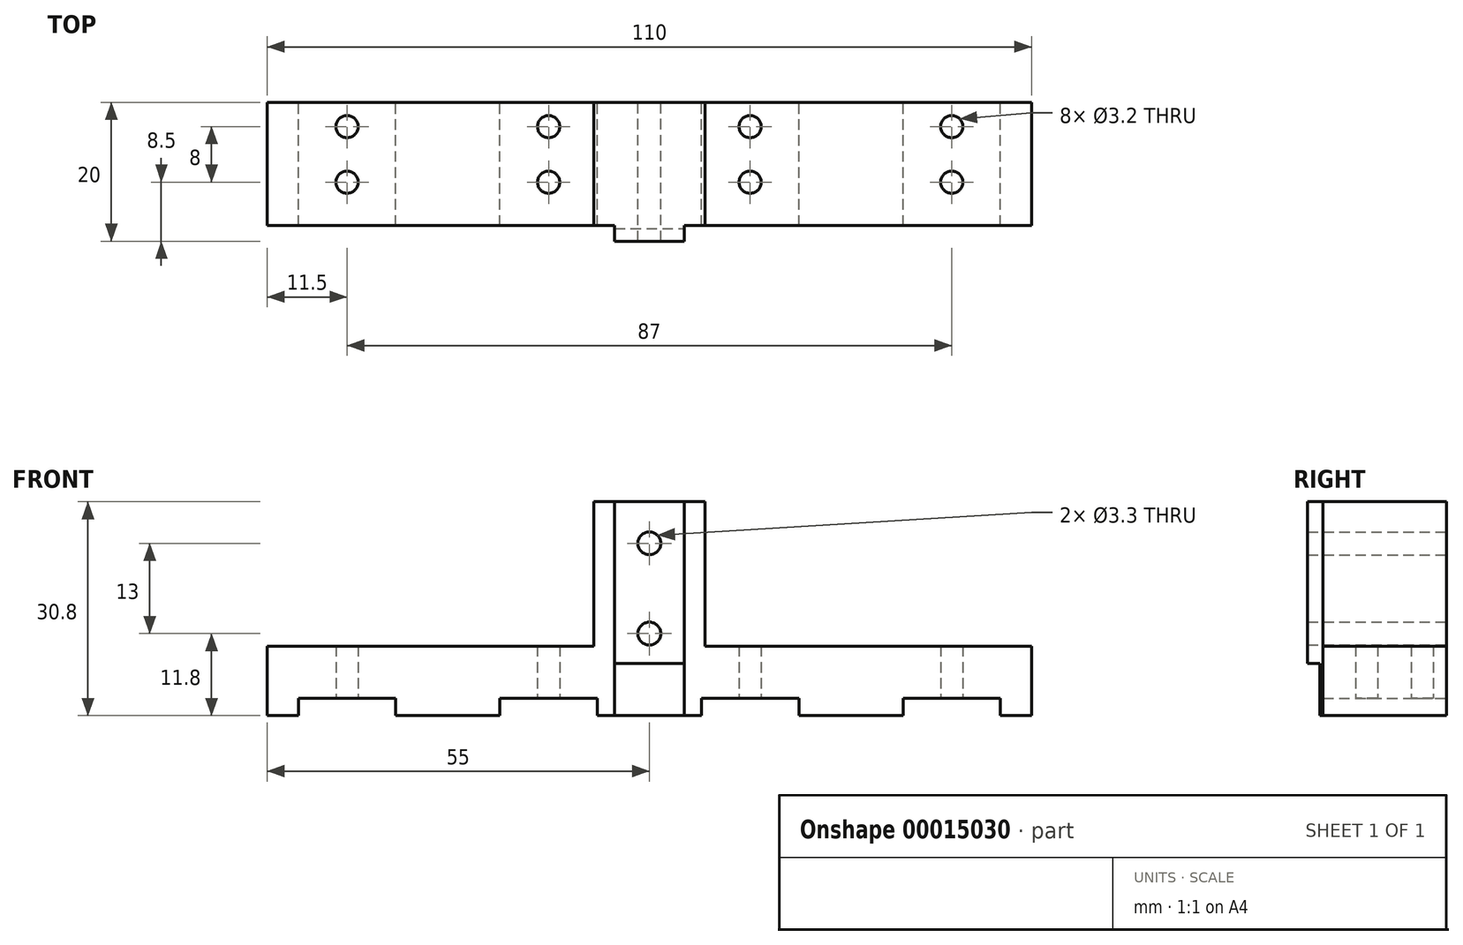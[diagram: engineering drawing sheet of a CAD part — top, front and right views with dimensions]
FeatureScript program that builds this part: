
annotation { "Feature Type Name" : "Feature", "Feature Type Description" : "" }
export const myFeature = defineFeature(function(context is Context, id is Id, definition is map)
    precondition{}
    {
        {
            var Q0;
            Q0=qCreatedBy(makeId("Front.planeOp"),FACE);
            var sketch = newSketch(context, id + "F0", { "sketchPlane" : qUnion([Q0])});
            skLineSegment(sketch, "E0", {"start": v(8, 20.8) * mm, "end": v(-8, 20.8) * mm});
            skLineSegment(sketch, "E1", {"start": v(-8, 20.8) * mm, "end": v(-8, 0) * mm});
            skLineSegment(sketch, "E2", {"start": v(-8, 0) * mm, "end": v(-55, 0) * mm});
            skLineSegment(sketch, "E3", {"start": v(-55, 0) * mm, "end": v(-55, -10) * mm});
            skLineSegment(sketch, "E4", {"start": v(-55, -10) * mm, "end": v(-50.5, -10) * mm});
            skLineSegment(sketch, "E5", {"start": v(-50.5, -10) * mm, "end": v(-50.5, -7.5) * mm});
            skLineSegment(sketch, "E6", {"start": v(-50.5, -7.5) * mm, "end": v(-36.5, -7.5) * mm});
            skLineSegment(sketch, "E7", {"start": v(-36.5, -7.5) * mm, "end": v(-36.5, -10) * mm});
            skLineSegment(sketch, "E8", {"start": v(-36.5, -10) * mm, "end": v(-21.5, -10) * mm});
            skLineSegment(sketch, "E9", {"start": v(-21.5, -10) * mm, "end": v(-21.5, -7.5) * mm});
            skLineSegment(sketch, "E10", {"start": v(-21.5, -7.5) * mm, "end": v(-7.5, -7.5) * mm});
            skLineSegment(sketch, "E11", {"start": v(-7.5, -7.5) * mm, "end": v(-7.5, -10) * mm});
            skLineSegment(sketch, "E12", {"start": v(-7.5, -10) * mm, "end": v(7.5, -10) * mm});
            skLineSegment(sketch, "E13", {"start": v(7.5, -10) * mm, "end": v(7.5, -7.5) * mm});
            skLineSegment(sketch, "E14", {"start": v(7.5, -7.5) * mm, "end": v(21.5, -7.5) * mm});
            skLineSegment(sketch, "E15", {"start": v(21.5, -7.5) * mm, "end": v(21.5, -10) * mm});
            skLineSegment(sketch, "E16", {"start": v(21.5, -10) * mm, "end": v(36.5, -10) * mm});
            skLineSegment(sketch, "E17", {"start": v(36.5, -10) * mm, "end": v(36.5, -7.5) * mm});
            skLineSegment(sketch, "E18", {"start": v(36.5, -7.5) * mm, "end": v(50.5, -7.5) * mm});
            skLineSegment(sketch, "E19", {"start": v(50.5, -7.5) * mm, "end": v(50.5, -10) * mm});
            skLineSegment(sketch, "E20", {"start": v(50.5, -10) * mm, "end": v(55, -10) * mm});
            skLineSegment(sketch, "E21", {"start": v(55, -10) * mm, "end": v(55, 0) * mm});
            skLineSegment(sketch, "E22", {"start": v(55, 0) * mm, "end": v(8, 0) * mm});
            skLineSegment(sketch, "E23", {"start": v(8, 0) * mm, "end": v(8, 20.8) * mm});
            skLineSegment(sketch, "E24", {"start": v(8, 20.8) * mm, "end": v(8, 20.8) * mm});
            skCircle(sketch, "E25", {"center": v(0, 1.8) * mm, "radius": 1.65 * mm});
            skCircle(sketch, "E26", {"center": v(0, 14.8) * mm, "radius": 1.65 * mm});
            skSolve(sketch);
        }
        {
            var Q0;
            Q0=makeQuery(id+"F0.imprint","IMPRINT",FACE,{"disambiguationData":[TD([[makeQuery(id+"F0.imprint","IMPRINT",EDGE,{"derivedFrom":sQuery(id+"F0.wireOp",EDGE,"E0")}),1.0]])]});
            extrude(context, id + "F1", {"entities" : qUnion([Q0]), "depth" : 17.75 * mm});
        }
        {
            var Q0;
            Q0=makeQuery(id+"F1.opExtrude","SWEPT_FACE",FACE,{"disambiguationData":[OSD([sQuery(id+"F0.wireOp",EDGE,"E6")])]});
            var sketch = newSketch(context, id + "F2", { "sketchPlane" : qUnion([Q0])});
            skPoint(sketch, "E27", {"position": v(-43.5, 11.5) * mm});
            skPoint(sketch, "E28", {"position": v(-43.5, 3.5) * mm});
            skPoint(sketch, "E29", {"position": v(-14.5, 11.5) * mm});
            skPoint(sketch, "E30", {"position": v(-14.5, 3.5) * mm});
            skPoint(sketch, "E31", {"position": v(14.5, 11.5) * mm});
            skPoint(sketch, "E32", {"position": v(14.5, 3.5) * mm});
            skPoint(sketch, "E33", {"position": v(43.5, 11.5) * mm});
            skPoint(sketch, "E34", {"position": v(43.5, 3.5) * mm});
            skSolve(sketch);
        }
        {
            var Q0;
            Q0=sQuery(id+"F2.wireOp",VERTEX,"E27");
            var Q1;
            Q1=sQuery(id+"F2.wireOp",VERTEX,"E28");
            var Q2;
            Q2=sQuery(id+"F2.wireOp",VERTEX,"E30");
            var Q3;
            Q3=sQuery(id+"F2.wireOp",VERTEX,"E29");
            var Q4;
            Q4=sQuery(id+"F2.wireOp",VERTEX,"E31");
            var Q5;
            Q5=sQuery(id+"F2.wireOp",VERTEX,"E32");
            var Q6;
            Q6=sQuery(id+"F2.wireOp",VERTEX,"E33");
            var Q7;
            Q7=sQuery(id+"F2.wireOp",VERTEX,"E34");
            var Q8;
            Q8=makeQuery(id+"F1.opExtrude","SWEPT_BODY",BODY,{"disambiguationData":[OSD([sQuery(id+"F0.wireOp",EDGE,"E0"),sQuery(id+"F0.wireOp",EDGE,"E1"),sQuery(id+"F0.wireOp",EDGE,"E2"),sQuery(id+"F0.wireOp",EDGE,"E3"),sQuery(id+"F0.wireOp",EDGE,"E4"),sQuery(id+"F0.wireOp",EDGE,"E5"),sQuery(id+"F0.wireOp",EDGE,"E6"),sQuery(id+"F0.wireOp",EDGE,"E7"),sQuery(id+"F0.wireOp",EDGE,"E8"),sQuery(id+"F0.wireOp",EDGE,"E9"),sQuery(id+"F0.wireOp",EDGE,"E10"),sQuery(id+"F0.wireOp",EDGE,"E11"),sQuery(id+"F0.wireOp",EDGE,"E12"),sQuery(id+"F0.wireOp",EDGE,"E13"),sQuery(id+"F0.wireOp",EDGE,"E14"),sQuery(id+"F0.wireOp",EDGE,"E15"),sQuery(id+"F0.wireOp",EDGE,"E16"),sQuery(id+"F0.wireOp",EDGE,"E17"),sQuery(id+"F0.wireOp",EDGE,"E18"),sQuery(id+"F0.wireOp",EDGE,"E19"),sQuery(id+"F0.wireOp",EDGE,"E20"),sQuery(id+"F0.wireOp",EDGE,"E21"),sQuery(id+"F0.wireOp",EDGE,"E22"),sQuery(id+"F0.wireOp",EDGE,"E23"),sQuery(id+"F0.wireOp",EDGE,"E25"),sQuery(id+"F0.wireOp",EDGE,"E26")])]});
            hole(context, id + "F3", {"style" : HoleStyle.SIMPLE, "holeDiameter" : 3.2 * mm, "endStyle" : HoleEndStyle.THROUGH, "locations" : qUnion([Q0, Q1, Q2, Q3, Q4, Q5, Q6, Q7]), "scope" : qUnion([Q8])});
        }
        {
            var Q0;
            Q0=makeQuery(id+"F1.opExtrude","CAP_FACE",FACE,{"disambiguationData":[OSD([sQuery(id+"F0.wireOp",EDGE,"E0"),sQuery(id+"F0.wireOp",EDGE,"E1"),sQuery(id+"F0.wireOp",EDGE,"E2"),sQuery(id+"F0.wireOp",EDGE,"E3"),sQuery(id+"F0.wireOp",EDGE,"E4"),sQuery(id+"F0.wireOp",EDGE,"E5"),sQuery(id+"F0.wireOp",EDGE,"E6"),sQuery(id+"F0.wireOp",EDGE,"E7"),sQuery(id+"F0.wireOp",EDGE,"E8"),sQuery(id+"F0.wireOp",EDGE,"E9"),sQuery(id+"F0.wireOp",EDGE,"E10"),sQuery(id+"F0.wireOp",EDGE,"E11"),sQuery(id+"F0.wireOp",EDGE,"E12"),sQuery(id+"F0.wireOp",EDGE,"E13"),sQuery(id+"F0.wireOp",EDGE,"E14"),sQuery(id+"F0.wireOp",EDGE,"E15"),sQuery(id+"F0.wireOp",EDGE,"E16"),sQuery(id+"F0.wireOp",EDGE,"E17"),sQuery(id+"F0.wireOp",EDGE,"E18"),sQuery(id+"F0.wireOp",EDGE,"E19"),sQuery(id+"F0.wireOp",EDGE,"E20"),sQuery(id+"F0.wireOp",EDGE,"E21"),sQuery(id+"F0.wireOp",EDGE,"E22"),sQuery(id+"F0.wireOp",EDGE,"E23"),sQuery(id+"F0.wireOp",EDGE,"E25"),sQuery(id+"F0.wireOp",EDGE,"E26")])],"isStart":false});
            var sketch = newSketch(context, id + "F4", { "sketchPlane" : qUnion([Q0])});
            skLineSegment(sketch, "E35.bottom", {"start": v(-5, 20.8) * mm, "end": v(5, 20.8) * mm});
            skLineSegment(sketch, "E35.top", {"start": v(-5, -2.5) * mm, "end": v(5, -2.5) * mm});
            skLineSegment(sketch, "E35.left", {"start": v(-5, 20.8) * mm, "end": v(-5, -2.5) * mm});
            skLineSegment(sketch, "E35.right", {"start": v(5, 20.8) * mm, "end": v(5, -2.5) * mm});
            skLineSegment(sketch, "E36.top", {"start": v(-5, -10) * mm, "end": v(5, -10) * mm});
            skLineSegment(sketch, "E36.left", {"start": v(-5, -2.5) * mm, "end": v(-5, -10) * mm});
            skLineSegment(sketch, "E36.right", {"start": v(5, -2.5) * mm, "end": v(5, -10) * mm});
            skSolve(sketch);
        }
        {
            var Q0;
            Q0=makeQuery(id+"F4.imprint","IMPRINT",FACE,{"disambiguationData":[TD([[makeQuery(id+"F4.imprint","IMPRINT",EDGE,{"derivedFrom":sQuery(id+"F4.wireOp",EDGE,"E35.bottom")}),1.0]])]});
            extrude(context, id + "F5", {"entities" : qUnion([Q0]), "operationType" : NewBodyOperationType.ADD, "depth" : 2.25 * mm});
        }
        {
            var Q0;
            Q0=makeQuery(id+"F4.imprint","IMPRINT",FACE,{"disambiguationData":[TD([[makeQuery(id+"F4.imprint","IMPRINT",EDGE,{"derivedFrom":sQuery(id+"F4.wireOp",EDGE,"E35.top")}),-1.0]])]});
            extrude(context, id + "F6", {"entities" : qUnion([Q0]), "operationType" : NewBodyOperationType.ADD, "depth" : 0.45 * mm});
        }
    });
